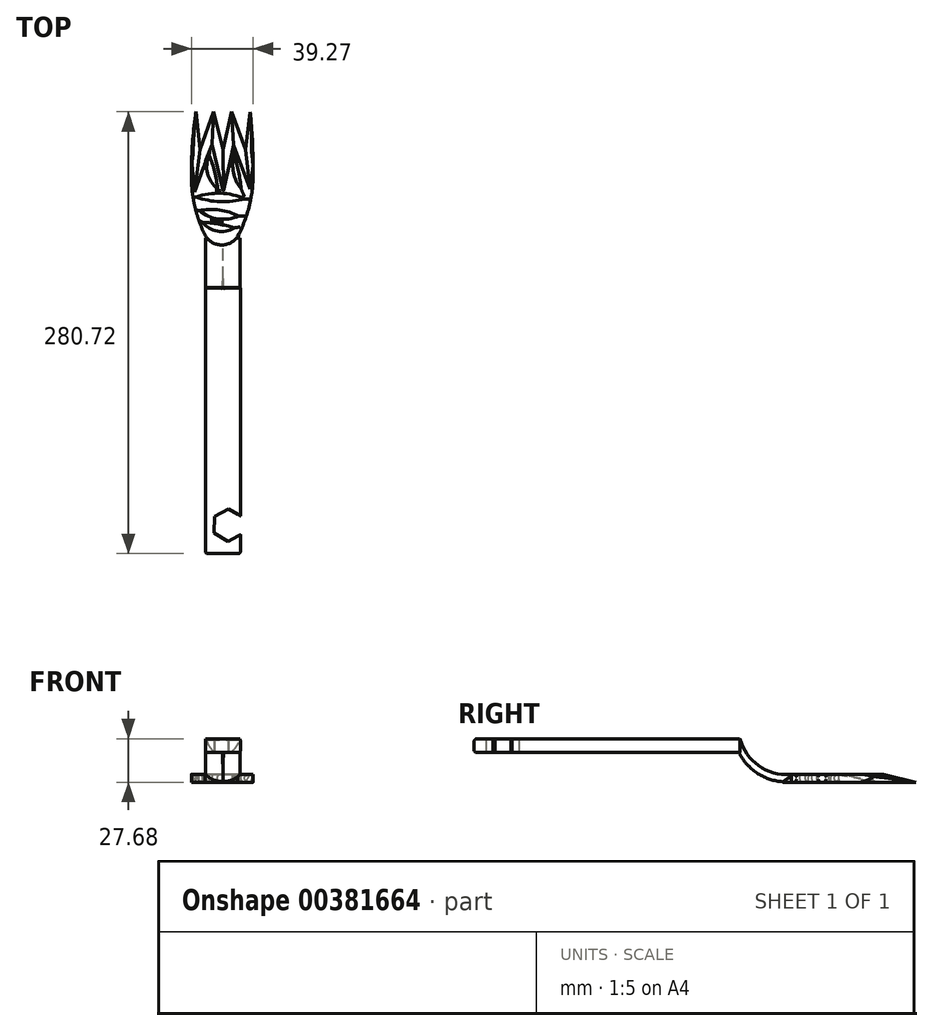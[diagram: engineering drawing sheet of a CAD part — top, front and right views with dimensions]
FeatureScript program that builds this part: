
annotation { "Feature Type Name" : "Feature", "Feature Type Description" : "" }
export const myFeature = defineFeature(function(context is Context, id is Id, definition is map)
    precondition{}
    {
        {
            var Q0;
            Q0=qCreatedBy(makeId("Top.planeOp"),FACE);
            var sketch = newSketch(context, id + "F0", { "sketchPlane" : qUnion([Q0])});
            skArc(sketch, "E0", {"start": v(-17.06, 76.18) * mm, "mid": v(-19.16, 58.5) * mm, "end": v(-19.86, 40.7) * mm});
            skArc(sketch, "E1", {"start": v(19.16, 40.7) * mm, "mid": v(18.71, 58.34) * mm, "end": v(17.35, 75.93) * mm});
            skLineSegment(sketch, "E2", {"start": v(-17.06, 76.18) * mm, "end": v(-14.55, 52.2) * mm});
            skLineSegment(sketch, "E3", {"start": v(14.3, 52.2) * mm, "end": v(17.35, 75.93) * mm});
            skLineSegment(sketch, "E4", {"start": v(-14.55, 52.2) * mm, "end": v(-5.87, 76.18) * mm});
            skLineSegment(sketch, "E5", {"start": v(-5.87, 76.18) * mm, "end": v(0, 52.2) * mm});
            skLineSegment(sketch, "E6", {"start": v(0, 52.2) * mm, "end": v(5.36, 76.18) * mm});
            skLineSegment(sketch, "E7", {"start": v(5.36, 76.18) * mm, "end": v(14.3, 52.2) * mm});
            skPoint(sketch, "E8.startSnap0", {"position": v(-19.86, 40.96) * mm});
            skPoint(sketch, "E9.orphan", {"position": v(19.16, 40.7) * mm});
            skArc(sketch, "E10", {"start": v(9.44, -3.2) * mm, "mid": v(17.18, 18.12) * mm, "end": v(19.16, 40.7) * mm});
            skArc(sketch, "E11", {"start": v(-19.86, 40.7) * mm, "mid": v(-18.37, 18.45) * mm, "end": v(-11.23, -2.68) * mm});
            skArc(sketch, "E12", {"start": v(-11.23, -2.68) * mm, "mid": v(-1.03, -8.6) * mm, "end": v(9.44, -3.2) * mm});
            skSolve(sketch);
        }
        {
            var Q0;
            Q0 = qSketchRegion(id + "F0", true);
            extrude(context, id + "F1", {"entities" : qUnion([Q0]), "endBound" : BoundingType.SYMMETRIC, "depth" : 5.08 * mm});
        }
        {
            var Q0;
            Q0=makeQuery(id+"F1.opExtrude","CAP_EDGE",EDGE,{"disambiguationData":[OSD([sQuery(id+"F0.wireOp",EDGE,"E1")])],"isStart":false});
            var Q1;
            Q1=makeQuery(id+"F1.opExtrude","CAP_EDGE",EDGE,{"disambiguationData":[OSD([sQuery(id+"F0.wireOp",EDGE,"E7")])],"isStart":false});
            var Q2;
            Q2=makeQuery(id+"F1.opExtrude","CAP_EDGE",EDGE,{"disambiguationData":[OSD([sQuery(id+"F0.wireOp",EDGE,"E3")])],"isStart":false});
            var Q3;
            Q3=makeQuery(id+"F1.opExtrude","CAP_EDGE",EDGE,{"disambiguationData":[OSD([sQuery(id+"F0.wireOp",EDGE,"E6")])],"isStart":false});
            var Q4;
            Q4=makeQuery(id+"F1.opExtrude","CAP_EDGE",EDGE,{"disambiguationData":[OSD([sQuery(id+"F0.wireOp",EDGE,"E5")])],"isStart":false});
            var Q5;
            Q5=makeQuery(id+"F1.opExtrude","CAP_EDGE",EDGE,{"disambiguationData":[OSD([sQuery(id+"F0.wireOp",EDGE,"E4")])],"isStart":false});
            var Q6;
            Q6=makeQuery(id+"F1.opExtrude","CAP_EDGE",EDGE,{"disambiguationData":[OSD([sQuery(id+"F0.wireOp",EDGE,"E2")])],"isStart":false});
            var Q7;
            Q7=makeQuery(id+"F1.opExtrude","CAP_EDGE",EDGE,{"disambiguationData":[OSD([sQuery(id+"F0.wireOp",EDGE,"E0")])],"isStart":false});
            chamfer(context, id + "F2", {"entities" : qUnion([Q0, Q1, Q2, Q3, Q4, Q5, Q6, Q7]), "chamferType" : ChamferType.TWO_OFFSETS, "width1" : 5.08 * mm, "oppositeDirection" : true, "width2" : 1.02 * mm, "tangentPropagation" : true});
        }
        {
            var Q0;
            {var subQ0=sQuery(id+"F0.wireOp",EDGE,"E5");Q0=makeQuery(id+"F2.opChamfer","BLEND_EDGE",EDGE,{"blendedFrom":[makeQuery(id+"F1.opExtrude","CAP_EDGE",EDGE,{"disambiguationData":[OSD([subQ0])],"isStart":false}),makeQuery(id+"F1.opExtrude","CAP_FACE",FACE,{"disambiguationData":[OSD([sQuery(id+"F0.wireOp",EDGE,"E0"),sQuery(id+"F0.wireOp",EDGE,"E1"),sQuery(id+"F0.wireOp",EDGE,"E2"),sQuery(id+"F0.wireOp",EDGE,"E3"),sQuery(id+"F0.wireOp",EDGE,"E4"),subQ0,sQuery(id+"F0.wireOp",EDGE,"E6"),sQuery(id+"F0.wireOp",EDGE,"E7"),sQuery(id+"F0.wireOp",EDGE,"E10"),sQuery(id+"F0.wireOp",EDGE,"E11"),sQuery(id+"F0.wireOp",EDGE,"E12")])],"isStart":false})],"blendedInto":[makeQuery(id+"F1.opExtrude","CAP_FACE",FACE,{"disambiguationData":[OSD([sQuery(id+"F0.wireOp",EDGE,"E0"),sQuery(id+"F0.wireOp",EDGE,"E1"),sQuery(id+"F0.wireOp",EDGE,"E2"),sQuery(id+"F0.wireOp",EDGE,"E3"),sQuery(id+"F0.wireOp",EDGE,"E4"),subQ0,sQuery(id+"F0.wireOp",EDGE,"E6"),sQuery(id+"F0.wireOp",EDGE,"E7"),sQuery(id+"F0.wireOp",EDGE,"E10"),sQuery(id+"F0.wireOp",EDGE,"E11"),sQuery(id+"F0.wireOp",EDGE,"E12")])],"isStart":false})]});}
            var Q1;
            {var subQ0=sQuery(id+"F0.wireOp",EDGE,"E4");Q1=makeQuery(id+"F2.opChamfer","BLEND_EDGE",EDGE,{"blendedFrom":[makeQuery(id+"F1.opExtrude","CAP_EDGE",EDGE,{"disambiguationData":[OSD([subQ0])],"isStart":false}),makeQuery(id+"F1.opExtrude","CAP_FACE",FACE,{"disambiguationData":[OSD([sQuery(id+"F0.wireOp",EDGE,"E0"),sQuery(id+"F0.wireOp",EDGE,"E1"),sQuery(id+"F0.wireOp",EDGE,"E2"),sQuery(id+"F0.wireOp",EDGE,"E3"),subQ0,sQuery(id+"F0.wireOp",EDGE,"E5"),sQuery(id+"F0.wireOp",EDGE,"E6"),sQuery(id+"F0.wireOp",EDGE,"E7"),sQuery(id+"F0.wireOp",EDGE,"E10"),sQuery(id+"F0.wireOp",EDGE,"E11"),sQuery(id+"F0.wireOp",EDGE,"E12")])],"isStart":false})],"blendedInto":[makeQuery(id+"F1.opExtrude","CAP_FACE",FACE,{"disambiguationData":[OSD([sQuery(id+"F0.wireOp",EDGE,"E0"),sQuery(id+"F0.wireOp",EDGE,"E1"),sQuery(id+"F0.wireOp",EDGE,"E2"),sQuery(id+"F0.wireOp",EDGE,"E3"),subQ0,sQuery(id+"F0.wireOp",EDGE,"E5"),sQuery(id+"F0.wireOp",EDGE,"E6"),sQuery(id+"F0.wireOp",EDGE,"E7"),sQuery(id+"F0.wireOp",EDGE,"E10"),sQuery(id+"F0.wireOp",EDGE,"E11"),sQuery(id+"F0.wireOp",EDGE,"E12")])],"isStart":false})]});}
            var Q2;
            {var subQ0=sQuery(id+"F0.wireOp",EDGE,"E6");Q2=makeQuery(id+"F2.opChamfer","BLEND_EDGE",EDGE,{"blendedFrom":[makeQuery(id+"F1.opExtrude","CAP_EDGE",EDGE,{"disambiguationData":[OSD([subQ0])],"isStart":false}),makeQuery(id+"F1.opExtrude","CAP_FACE",FACE,{"disambiguationData":[OSD([sQuery(id+"F0.wireOp",EDGE,"E0"),sQuery(id+"F0.wireOp",EDGE,"E1"),sQuery(id+"F0.wireOp",EDGE,"E2"),sQuery(id+"F0.wireOp",EDGE,"E3"),sQuery(id+"F0.wireOp",EDGE,"E4"),sQuery(id+"F0.wireOp",EDGE,"E5"),subQ0,sQuery(id+"F0.wireOp",EDGE,"E7"),sQuery(id+"F0.wireOp",EDGE,"E10"),sQuery(id+"F0.wireOp",EDGE,"E11"),sQuery(id+"F0.wireOp",EDGE,"E12")])],"isStart":false})],"blendedInto":[makeQuery(id+"F1.opExtrude","CAP_FACE",FACE,{"disambiguationData":[OSD([sQuery(id+"F0.wireOp",EDGE,"E0"),sQuery(id+"F0.wireOp",EDGE,"E1"),sQuery(id+"F0.wireOp",EDGE,"E2"),sQuery(id+"F0.wireOp",EDGE,"E3"),sQuery(id+"F0.wireOp",EDGE,"E4"),sQuery(id+"F0.wireOp",EDGE,"E5"),subQ0,sQuery(id+"F0.wireOp",EDGE,"E7"),sQuery(id+"F0.wireOp",EDGE,"E10"),sQuery(id+"F0.wireOp",EDGE,"E11"),sQuery(id+"F0.wireOp",EDGE,"E12")])],"isStart":false})]});}
            var Q3;
            {var subQ0=sQuery(id+"F0.wireOp",EDGE,"E7");Q3=makeQuery(id+"F2.opChamfer","BLEND_EDGE",EDGE,{"blendedFrom":[makeQuery(id+"F1.opExtrude","CAP_EDGE",EDGE,{"disambiguationData":[OSD([subQ0])],"isStart":false}),makeQuery(id+"F1.opExtrude","CAP_FACE",FACE,{"disambiguationData":[OSD([sQuery(id+"F0.wireOp",EDGE,"E0"),sQuery(id+"F0.wireOp",EDGE,"E1"),sQuery(id+"F0.wireOp",EDGE,"E2"),sQuery(id+"F0.wireOp",EDGE,"E3"),sQuery(id+"F0.wireOp",EDGE,"E4"),sQuery(id+"F0.wireOp",EDGE,"E5"),sQuery(id+"F0.wireOp",EDGE,"E6"),subQ0,sQuery(id+"F0.wireOp",EDGE,"E10"),sQuery(id+"F0.wireOp",EDGE,"E11"),sQuery(id+"F0.wireOp",EDGE,"E12")])],"isStart":false})],"blendedInto":[makeQuery(id+"F1.opExtrude","CAP_FACE",FACE,{"disambiguationData":[OSD([sQuery(id+"F0.wireOp",EDGE,"E0"),sQuery(id+"F0.wireOp",EDGE,"E1"),sQuery(id+"F0.wireOp",EDGE,"E2"),sQuery(id+"F0.wireOp",EDGE,"E3"),sQuery(id+"F0.wireOp",EDGE,"E4"),sQuery(id+"F0.wireOp",EDGE,"E5"),sQuery(id+"F0.wireOp",EDGE,"E6"),subQ0,sQuery(id+"F0.wireOp",EDGE,"E10"),sQuery(id+"F0.wireOp",EDGE,"E11"),sQuery(id+"F0.wireOp",EDGE,"E12")])],"isStart":false})]});}
            var Q4;
            {var subQ0=sQuery(id+"F0.wireOp",EDGE,"E3");Q4=makeQuery(id+"F2.opChamfer","BLEND_EDGE",EDGE,{"blendedFrom":[makeQuery(id+"F1.opExtrude","CAP_EDGE",EDGE,{"disambiguationData":[OSD([subQ0])],"isStart":false}),makeQuery(id+"F1.opExtrude","CAP_FACE",FACE,{"disambiguationData":[OSD([sQuery(id+"F0.wireOp",EDGE,"E0"),sQuery(id+"F0.wireOp",EDGE,"E1"),sQuery(id+"F0.wireOp",EDGE,"E2"),subQ0,sQuery(id+"F0.wireOp",EDGE,"E4"),sQuery(id+"F0.wireOp",EDGE,"E5"),sQuery(id+"F0.wireOp",EDGE,"E6"),sQuery(id+"F0.wireOp",EDGE,"E7"),sQuery(id+"F0.wireOp",EDGE,"E10"),sQuery(id+"F0.wireOp",EDGE,"E11"),sQuery(id+"F0.wireOp",EDGE,"E12")])],"isStart":false})],"blendedInto":[makeQuery(id+"F1.opExtrude","CAP_FACE",FACE,{"disambiguationData":[OSD([sQuery(id+"F0.wireOp",EDGE,"E0"),sQuery(id+"F0.wireOp",EDGE,"E1"),sQuery(id+"F0.wireOp",EDGE,"E2"),subQ0,sQuery(id+"F0.wireOp",EDGE,"E4"),sQuery(id+"F0.wireOp",EDGE,"E5"),sQuery(id+"F0.wireOp",EDGE,"E6"),sQuery(id+"F0.wireOp",EDGE,"E7"),sQuery(id+"F0.wireOp",EDGE,"E10"),sQuery(id+"F0.wireOp",EDGE,"E11"),sQuery(id+"F0.wireOp",EDGE,"E12")])],"isStart":false})]});}
            var Q5;
            {var subQ0=sQuery(id+"F0.wireOp",EDGE,"E2");Q5=makeQuery(id+"F2.opChamfer","BLEND_EDGE",EDGE,{"blendedFrom":[makeQuery(id+"F1.opExtrude","CAP_EDGE",EDGE,{"disambiguationData":[OSD([subQ0])],"isStart":false}),makeQuery(id+"F1.opExtrude","CAP_FACE",FACE,{"disambiguationData":[OSD([sQuery(id+"F0.wireOp",EDGE,"E0"),sQuery(id+"F0.wireOp",EDGE,"E1"),subQ0,sQuery(id+"F0.wireOp",EDGE,"E3"),sQuery(id+"F0.wireOp",EDGE,"E4"),sQuery(id+"F0.wireOp",EDGE,"E5"),sQuery(id+"F0.wireOp",EDGE,"E6"),sQuery(id+"F0.wireOp",EDGE,"E7"),sQuery(id+"F0.wireOp",EDGE,"E10"),sQuery(id+"F0.wireOp",EDGE,"E11"),sQuery(id+"F0.wireOp",EDGE,"E12")])],"isStart":false})],"blendedInto":[makeQuery(id+"F1.opExtrude","CAP_FACE",FACE,{"disambiguationData":[OSD([sQuery(id+"F0.wireOp",EDGE,"E0"),sQuery(id+"F0.wireOp",EDGE,"E1"),subQ0,sQuery(id+"F0.wireOp",EDGE,"E3"),sQuery(id+"F0.wireOp",EDGE,"E4"),sQuery(id+"F0.wireOp",EDGE,"E5"),sQuery(id+"F0.wireOp",EDGE,"E6"),sQuery(id+"F0.wireOp",EDGE,"E7"),sQuery(id+"F0.wireOp",EDGE,"E10"),sQuery(id+"F0.wireOp",EDGE,"E11"),sQuery(id+"F0.wireOp",EDGE,"E12")])],"isStart":false})]});}
            chamfer(context, id + "F3", {"entities" : qUnion([Q0, Q1, Q2, Q3, Q4, Q5]), "chamferType" : ChamferType.OFFSET_ANGLE, "width" : 5.08 * mm, "oppositeDirection" : false, "angle" : 40 * degree, "tangentPropagation" : true});
        }
        {
            var Q0;
            Q0=qCreatedBy(makeId("Right.planeOp"),FACE);
            var sketch = newSketch(context, id + "F4", { "sketchPlane" : qUnion([Q0])});
            skArc(sketch, "E13", {"start": v(-36.75, 16.97) * mm, "mid": v(-23.48, 2.4) * mm, "end": v(-4.31, -2.22) * mm});
            skArc(sketch, "E14", {"start": v(-35.73, 25.14) * mm, "mid": v(-24, 8.07) * mm, "end": v(-4.07, 2.39) * mm});
            skLineSegment(sketch, "E15", {"start": v(-35.73, 25.14) * mm, "end": v(-36.75, 16.97) * mm});
            skLineSegment(sketch, "E16", {"start": v(-4.07, 2.39) * mm, "end": v(-4.31, -2.22) * mm});
            skSolve(sketch);
        }
        {
            var Q0;
            Q0 = qSketchRegion(id + "F4", true);
            extrude(context, id + "F5", {"entities" : qUnion([Q0]), "operationType" : NewBodyOperationType.ADD, "endBound" : BoundingType.SYMMETRIC, "depth" : 21.84 * mm});
        }
        {
            var Q0;
            Q0=qCreatedBy(makeId("Right.planeOp"),FACE);
            var sketch = newSketch(context, id + "F6", { "sketchPlane" : qUnion([Q0])});
            skLineSegment(sketch, "E17.bottom", {"start": v(-35.8, 24.94) * mm, "end": v(-204.68, 24.94) * mm});
            skLineSegment(sketch, "E17.top", {"start": v(-35.8, 16.37) * mm, "end": v(-204.68, 16.37) * mm});
            skLineSegment(sketch, "E17.left", {"start": v(-35.8, 24.94) * mm, "end": v(-35.8, 16.37) * mm});
            skLineSegment(sketch, "E17.right", {"start": v(-204.68, 24.94) * mm, "end": v(-204.68, 16.37) * mm});
            skSolve(sketch);
        }
        {
            var Q0;
            Q0 = qSketchRegion(id + "F6", true);
            extrude(context, id + "F7", {"entities" : qUnion([Q0]), "operationType" : NewBodyOperationType.ADD, "endBound" : BoundingType.SYMMETRIC, "depth" : 22.35 * mm});
        }
        {
            var Q0;
            Q0=makeQuery(id+"F5.opExtrude","CAP_EDGE",EDGE,{"disambiguationData":[OSD([sQuery(id+"F4.wireOp",EDGE,"E13")])],"isStart":true});
            var Q1;
            Q1=makeQuery(id+"F5.opExtrude","CAP_EDGE",EDGE,{"disambiguationData":[OSD([sQuery(id+"F4.wireOp",EDGE,"E13")])],"isStart":false});
            fillet(context, id + "F8", {"entities" : qUnion([Q0, Q1]), "radius" : 15.94 * mm, "tangentPropagation" : true, "allowEdgeOverflow" : false});
        }
        {
            var Q0;
            Q0=makeQuery(id+"F7.opExtrude","CAP_EDGE",EDGE,{"disambiguationData":[OSD([sQuery(id+"F6.wireOp",EDGE,"E17.bottom")])],"isStart":false});
            var Q1;
            Q1=makeQuery(id+"F7.opExtrude","CAP_EDGE",EDGE,{"disambiguationData":[OSD([sQuery(id+"F6.wireOp",EDGE,"E17.top")])],"isStart":false});
            var Q2;
            Q2=makeQuery(id+"F7.opExtrude","CAP_EDGE",EDGE,{"disambiguationData":[OSD([sQuery(id+"F6.wireOp",EDGE,"E17.bottom")])],"isStart":true});
            var Q3;
            Q3=makeQuery(id+"F7.opExtrude","CAP_EDGE",EDGE,{"disambiguationData":[OSD([sQuery(id+"F6.wireOp",EDGE,"E17.top")])],"isStart":true});
            var Q4;
            Q4=makeQuery(id+"F7.opExtrude","SWEPT_FACE",FACE,{"disambiguationData":[OSD([sQuery(id+"F6.wireOp",EDGE,"E17.right")])]});
            fillet(context, id + "F9", {"entities" : qUnion([Q0, Q1, Q2, Q3, Q4]), "radius" : 1.55 * mm, "tangentPropagation" : true, "allowEdgeOverflow" : false});
        }
        {
            var Q0;
            Q0=makeQuery(id+"F9.opFillet","BLEND_EDGE",EDGE,{"blendedFrom":[makeQuery(id+"F7.opExtrude","CAP_EDGE",EDGE,{"disambiguationData":[OSD([sQuery(id+"F6.wireOp",EDGE,"E17.top")])],"isStart":false}),makeQuery(id+"F7.opExtrude","SWEPT_FACE",FACE,{"disambiguationData":[OSD([sQuery(id+"F6.wireOp",EDGE,"E17.left")])]})],"blendedInto":[makeQuery(id+"F7.opExtrude","SWEPT_FACE",FACE,{"disambiguationData":[OSD([sQuery(id+"F6.wireOp",EDGE,"E17.left")])]})]});
            var Q1;
            Q1=makeQuery(id+"F9.opFillet","BLEND_EDGE",EDGE,{"blendedFrom":[makeQuery(id+"F7.opExtrude","CAP_EDGE",EDGE,{"disambiguationData":[OSD([sQuery(id+"F6.wireOp",EDGE,"E17.top")])],"isStart":true}),makeQuery(id+"F7.opExtrude","SWEPT_FACE",FACE,{"disambiguationData":[OSD([sQuery(id+"F6.wireOp",EDGE,"E17.left")])]})],"blendedInto":[makeQuery(id+"F7.opExtrude","SWEPT_FACE",FACE,{"disambiguationData":[OSD([sQuery(id+"F6.wireOp",EDGE,"E17.left")])]})]});
            fillet(context, id + "F10", {"entities" : qUnion([Q0, Q1]), "radius" : 0.5 * mm, "tangentPropagation" : true, "allowEdgeOverflow" : false});
        }
        {
            var Q0;
            Q0=qCreatedBy(makeId("Top.planeOp"),FACE);
            var sketch = newSketch(context, id + "F11", { "sketchPlane" : qUnion([Q0])});
            skArc(sketch, "E18", {"start": v(13.88, 20.7) * mm, "mid": v(-1.4, 24.24) * mm, "end": v(-16.91, 21.85) * mm});
            skArc(sketch, "E19", {"start": v(-16.91, 21.85) * mm, "mid": v(-1.6, 18.87) * mm, "end": v(13.88, 20.7) * mm});
            skArc(sketch, "E20", {"start": v(-8.66, 48.42) * mm, "mid": v(-9.75, 36.88) * mm, "end": v(-3.36, 27.2) * mm});
            skArc(sketch, "E21", {"start": v(-3.36, 27.2) * mm, "mid": v(-5.31, 37.99) * mm, "end": v(-8.66, 48.42) * mm});
            skArc(sketch, "E22", {"start": v(11.5, 27.2) * mm, "mid": v(9.97, 37.95) * mm, "end": v(7.14, 48.42) * mm});
            skArc(sketch, "E23", {"start": v(7.14, 48.42) * mm, "mid": v(6.72, 37.28) * mm, "end": v(11.5, 27.2) * mm});
            skArc(sketch, "E24", {"start": v(-15.07, 13.17) * mm, "mid": v(-2.94, 7.96) * mm, "end": v(10.12, 9.84) * mm});
            skArc(sketch, "E25", {"start": v(10.12, 9.84) * mm, "mid": v(-2.2, 13.6) * mm, "end": v(-15.07, 13.17) * mm});
            skArc(sketch, "E26", {"start": v(-12.9, 5.76) * mm, "mid": v(-3.55, 0.2) * mm, "end": v(7.14, 2.27) * mm});
            skArc(sketch, "E27", {"start": v(7.14, 2.27) * mm, "mid": v(-2.77, 4.68) * mm, "end": v(-12.9, 5.76) * mm});
            skSolve(sketch);
        }
        {
            var Q0;
            Q0 = qSketchRegion(id + "F11", true);
            extrude(context, id + "F12", {"entities" : qUnion([Q0]), "operationType" : NewBodyOperationType.REMOVE, "endBound" : BoundingType.SYMMETRIC, "oppositeDirection" : true, "depth" : 25.4 * mm});
        }
        {
            var Q0;
            Q0=makeQuery(id+"F12.boolean.opBoolean","INTERSECT",EDGE,{"derivedFrom":[makeQuery(id+"F1.opExtrude","CAP_FACE",FACE,{"disambiguationData":[OSD([sQuery(id+"F0.wireOp",EDGE,"E0"),sQuery(id+"F0.wireOp",EDGE,"E1"),sQuery(id+"F0.wireOp",EDGE,"E2"),sQuery(id+"F0.wireOp",EDGE,"E3"),sQuery(id+"F0.wireOp",EDGE,"E4"),sQuery(id+"F0.wireOp",EDGE,"E5"),sQuery(id+"F0.wireOp",EDGE,"E6"),sQuery(id+"F0.wireOp",EDGE,"E7"),sQuery(id+"F0.wireOp",EDGE,"E10"),sQuery(id+"F0.wireOp",EDGE,"E11"),sQuery(id+"F0.wireOp",EDGE,"E12")])],"isStart":false}),makeQuery(id+"F12.opExtrude","SWEPT_FACE",FACE,{"disambiguationData":[OSD([sQuery(id+"F11.wireOp",EDGE,"E20")])]})]});
            var Q1;
            Q1=makeQuery(id+"F12.boolean.opBoolean","INTERSECT",EDGE,{"derivedFrom":[makeQuery(id+"F1.opExtrude","CAP_FACE",FACE,{"disambiguationData":[OSD([sQuery(id+"F0.wireOp",EDGE,"E0"),sQuery(id+"F0.wireOp",EDGE,"E1"),sQuery(id+"F0.wireOp",EDGE,"E2"),sQuery(id+"F0.wireOp",EDGE,"E3"),sQuery(id+"F0.wireOp",EDGE,"E4"),sQuery(id+"F0.wireOp",EDGE,"E5"),sQuery(id+"F0.wireOp",EDGE,"E6"),sQuery(id+"F0.wireOp",EDGE,"E7"),sQuery(id+"F0.wireOp",EDGE,"E10"),sQuery(id+"F0.wireOp",EDGE,"E11"),sQuery(id+"F0.wireOp",EDGE,"E12")])],"isStart":false}),makeQuery(id+"F12.opExtrude","SWEPT_FACE",FACE,{"disambiguationData":[OSD([sQuery(id+"F11.wireOp",EDGE,"E21")])]})]});
            var Q2;
            Q2=makeQuery(id+"F12.boolean.opBoolean","INTERSECT",EDGE,{"derivedFrom":[makeQuery(id+"F1.opExtrude","CAP_FACE",FACE,{"disambiguationData":[OSD([sQuery(id+"F0.wireOp",EDGE,"E0"),sQuery(id+"F0.wireOp",EDGE,"E1"),sQuery(id+"F0.wireOp",EDGE,"E2"),sQuery(id+"F0.wireOp",EDGE,"E3"),sQuery(id+"F0.wireOp",EDGE,"E4"),sQuery(id+"F0.wireOp",EDGE,"E5"),sQuery(id+"F0.wireOp",EDGE,"E6"),sQuery(id+"F0.wireOp",EDGE,"E7"),sQuery(id+"F0.wireOp",EDGE,"E10"),sQuery(id+"F0.wireOp",EDGE,"E11"),sQuery(id+"F0.wireOp",EDGE,"E12")])],"isStart":false}),makeQuery(id+"F12.opExtrude","SWEPT_FACE",FACE,{"disambiguationData":[OSD([sQuery(id+"F11.wireOp",EDGE,"E22")])]})]});
            var Q3;
            Q3=makeQuery(id+"F12.boolean.opBoolean","INTERSECT",EDGE,{"derivedFrom":[makeQuery(id+"F1.opExtrude","CAP_FACE",FACE,{"disambiguationData":[OSD([sQuery(id+"F0.wireOp",EDGE,"E0"),sQuery(id+"F0.wireOp",EDGE,"E1"),sQuery(id+"F0.wireOp",EDGE,"E2"),sQuery(id+"F0.wireOp",EDGE,"E3"),sQuery(id+"F0.wireOp",EDGE,"E4"),sQuery(id+"F0.wireOp",EDGE,"E5"),sQuery(id+"F0.wireOp",EDGE,"E6"),sQuery(id+"F0.wireOp",EDGE,"E7"),sQuery(id+"F0.wireOp",EDGE,"E10"),sQuery(id+"F0.wireOp",EDGE,"E11"),sQuery(id+"F0.wireOp",EDGE,"E12")])],"isStart":false}),makeQuery(id+"F12.opExtrude","SWEPT_FACE",FACE,{"disambiguationData":[OSD([sQuery(id+"F11.wireOp",EDGE,"E23")])]})]});
            var Q4;
            Q4=makeQuery(id+"F12.boolean.opBoolean","INTERSECT",EDGE,{"derivedFrom":[makeQuery(id+"F1.opExtrude","CAP_FACE",FACE,{"disambiguationData":[OSD([sQuery(id+"F0.wireOp",EDGE,"E0"),sQuery(id+"F0.wireOp",EDGE,"E1"),sQuery(id+"F0.wireOp",EDGE,"E2"),sQuery(id+"F0.wireOp",EDGE,"E3"),sQuery(id+"F0.wireOp",EDGE,"E4"),sQuery(id+"F0.wireOp",EDGE,"E5"),sQuery(id+"F0.wireOp",EDGE,"E6"),sQuery(id+"F0.wireOp",EDGE,"E7"),sQuery(id+"F0.wireOp",EDGE,"E10"),sQuery(id+"F0.wireOp",EDGE,"E11"),sQuery(id+"F0.wireOp",EDGE,"E12")])],"isStart":false}),makeQuery(id+"F12.opExtrude","SWEPT_FACE",FACE,{"disambiguationData":[OSD([sQuery(id+"F11.wireOp",EDGE,"E19")])]})]});
            var Q5;
            Q5=makeQuery(id+"F12.boolean.opBoolean","INTERSECT",EDGE,{"derivedFrom":[makeQuery(id+"F1.opExtrude","CAP_FACE",FACE,{"disambiguationData":[OSD([sQuery(id+"F0.wireOp",EDGE,"E0"),sQuery(id+"F0.wireOp",EDGE,"E1"),sQuery(id+"F0.wireOp",EDGE,"E2"),sQuery(id+"F0.wireOp",EDGE,"E3"),sQuery(id+"F0.wireOp",EDGE,"E4"),sQuery(id+"F0.wireOp",EDGE,"E5"),sQuery(id+"F0.wireOp",EDGE,"E6"),sQuery(id+"F0.wireOp",EDGE,"E7"),sQuery(id+"F0.wireOp",EDGE,"E10"),sQuery(id+"F0.wireOp",EDGE,"E11"),sQuery(id+"F0.wireOp",EDGE,"E12")])],"isStart":false}),makeQuery(id+"F12.opExtrude","SWEPT_FACE",FACE,{"disambiguationData":[OSD([sQuery(id+"F11.wireOp",EDGE,"E18")])]})]});
            var Q6;
            Q6=makeQuery(id+"F12.boolean.opBoolean","INTERSECT",EDGE,{"derivedFrom":[makeQuery(id+"F1.opExtrude","CAP_FACE",FACE,{"disambiguationData":[OSD([sQuery(id+"F0.wireOp",EDGE,"E0"),sQuery(id+"F0.wireOp",EDGE,"E1"),sQuery(id+"F0.wireOp",EDGE,"E2"),sQuery(id+"F0.wireOp",EDGE,"E3"),sQuery(id+"F0.wireOp",EDGE,"E4"),sQuery(id+"F0.wireOp",EDGE,"E5"),sQuery(id+"F0.wireOp",EDGE,"E6"),sQuery(id+"F0.wireOp",EDGE,"E7"),sQuery(id+"F0.wireOp",EDGE,"E10"),sQuery(id+"F0.wireOp",EDGE,"E11"),sQuery(id+"F0.wireOp",EDGE,"E12")])],"isStart":false}),makeQuery(id+"F12.opExtrude","SWEPT_FACE",FACE,{"disambiguationData":[OSD([sQuery(id+"F11.wireOp",EDGE,"E25")])]})]});
            var Q7;
            Q7=makeQuery(id+"F12.boolean.opBoolean","INTERSECT",EDGE,{"derivedFrom":[makeQuery(id+"F1.opExtrude","CAP_FACE",FACE,{"disambiguationData":[OSD([sQuery(id+"F0.wireOp",EDGE,"E0"),sQuery(id+"F0.wireOp",EDGE,"E1"),sQuery(id+"F0.wireOp",EDGE,"E2"),sQuery(id+"F0.wireOp",EDGE,"E3"),sQuery(id+"F0.wireOp",EDGE,"E4"),sQuery(id+"F0.wireOp",EDGE,"E5"),sQuery(id+"F0.wireOp",EDGE,"E6"),sQuery(id+"F0.wireOp",EDGE,"E7"),sQuery(id+"F0.wireOp",EDGE,"E10"),sQuery(id+"F0.wireOp",EDGE,"E11"),sQuery(id+"F0.wireOp",EDGE,"E12")])],"isStart":false}),makeQuery(id+"F12.opExtrude","SWEPT_FACE",FACE,{"disambiguationData":[OSD([sQuery(id+"F11.wireOp",EDGE,"E24")])]})]});
            var Q8;
            Q8=makeQuery(id+"F12.boolean.opBoolean","INTERSECT",EDGE,{"derivedFrom":[makeQuery(id+"F1.opExtrude","CAP_FACE",FACE,{"disambiguationData":[OSD([sQuery(id+"F0.wireOp",EDGE,"E0"),sQuery(id+"F0.wireOp",EDGE,"E1"),sQuery(id+"F0.wireOp",EDGE,"E2"),sQuery(id+"F0.wireOp",EDGE,"E3"),sQuery(id+"F0.wireOp",EDGE,"E4"),sQuery(id+"F0.wireOp",EDGE,"E5"),sQuery(id+"F0.wireOp",EDGE,"E6"),sQuery(id+"F0.wireOp",EDGE,"E7"),sQuery(id+"F0.wireOp",EDGE,"E10"),sQuery(id+"F0.wireOp",EDGE,"E11"),sQuery(id+"F0.wireOp",EDGE,"E12")])],"isStart":false}),makeQuery(id+"F12.opExtrude","SWEPT_FACE",FACE,{"disambiguationData":[OSD([sQuery(id+"F11.wireOp",EDGE,"E27")])]})]});
            var Q9;
            Q9=makeQuery(id+"F12.boolean.opBoolean","INTERSECT",EDGE,{"derivedFrom":[makeQuery(id+"F1.opExtrude","CAP_FACE",FACE,{"disambiguationData":[OSD([sQuery(id+"F0.wireOp",EDGE,"E0"),sQuery(id+"F0.wireOp",EDGE,"E1"),sQuery(id+"F0.wireOp",EDGE,"E2"),sQuery(id+"F0.wireOp",EDGE,"E3"),sQuery(id+"F0.wireOp",EDGE,"E4"),sQuery(id+"F0.wireOp",EDGE,"E5"),sQuery(id+"F0.wireOp",EDGE,"E6"),sQuery(id+"F0.wireOp",EDGE,"E7"),sQuery(id+"F0.wireOp",EDGE,"E10"),sQuery(id+"F0.wireOp",EDGE,"E11"),sQuery(id+"F0.wireOp",EDGE,"E12")])],"isStart":false}),makeQuery(id+"F12.opExtrude","SWEPT_FACE",FACE,{"disambiguationData":[OSD([sQuery(id+"F11.wireOp",EDGE,"E26")])]})]});
            var Q10;
            Q10=makeQuery(id+"F12.boolean.opBoolean","INTERSECT",EDGE,{"derivedFrom":[makeQuery(id+"F1.opExtrude","CAP_FACE",FACE,{"disambiguationData":[OSD([sQuery(id+"F0.wireOp",EDGE,"E0"),sQuery(id+"F0.wireOp",EDGE,"E1"),sQuery(id+"F0.wireOp",EDGE,"E2"),sQuery(id+"F0.wireOp",EDGE,"E3"),sQuery(id+"F0.wireOp",EDGE,"E4"),sQuery(id+"F0.wireOp",EDGE,"E5"),sQuery(id+"F0.wireOp",EDGE,"E6"),sQuery(id+"F0.wireOp",EDGE,"E7"),sQuery(id+"F0.wireOp",EDGE,"E10"),sQuery(id+"F0.wireOp",EDGE,"E11"),sQuery(id+"F0.wireOp",EDGE,"E12")])],"isStart":true}),makeQuery(id+"F12.opExtrude","SWEPT_FACE",FACE,{"disambiguationData":[OSD([sQuery(id+"F11.wireOp",EDGE,"E23")])]})]});
            var Q11;
            Q11=makeQuery(id+"F12.boolean.opBoolean","INTERSECT",EDGE,{"derivedFrom":[makeQuery(id+"F1.opExtrude","CAP_FACE",FACE,{"disambiguationData":[OSD([sQuery(id+"F0.wireOp",EDGE,"E0"),sQuery(id+"F0.wireOp",EDGE,"E1"),sQuery(id+"F0.wireOp",EDGE,"E2"),sQuery(id+"F0.wireOp",EDGE,"E3"),sQuery(id+"F0.wireOp",EDGE,"E4"),sQuery(id+"F0.wireOp",EDGE,"E5"),sQuery(id+"F0.wireOp",EDGE,"E6"),sQuery(id+"F0.wireOp",EDGE,"E7"),sQuery(id+"F0.wireOp",EDGE,"E10"),sQuery(id+"F0.wireOp",EDGE,"E11"),sQuery(id+"F0.wireOp",EDGE,"E12")])],"isStart":true}),makeQuery(id+"F12.opExtrude","SWEPT_FACE",FACE,{"disambiguationData":[OSD([sQuery(id+"F11.wireOp",EDGE,"E22")])]})]});
            var Q12;
            Q12=makeQuery(id+"F12.boolean.opBoolean","INTERSECT",EDGE,{"derivedFrom":[makeQuery(id+"F1.opExtrude","CAP_FACE",FACE,{"disambiguationData":[OSD([sQuery(id+"F0.wireOp",EDGE,"E0"),sQuery(id+"F0.wireOp",EDGE,"E1"),sQuery(id+"F0.wireOp",EDGE,"E2"),sQuery(id+"F0.wireOp",EDGE,"E3"),sQuery(id+"F0.wireOp",EDGE,"E4"),sQuery(id+"F0.wireOp",EDGE,"E5"),sQuery(id+"F0.wireOp",EDGE,"E6"),sQuery(id+"F0.wireOp",EDGE,"E7"),sQuery(id+"F0.wireOp",EDGE,"E10"),sQuery(id+"F0.wireOp",EDGE,"E11"),sQuery(id+"F0.wireOp",EDGE,"E12")])],"isStart":true}),makeQuery(id+"F12.opExtrude","SWEPT_FACE",FACE,{"disambiguationData":[OSD([sQuery(id+"F11.wireOp",EDGE,"E21")])]})]});
            var Q13;
            Q13=makeQuery(id+"F12.boolean.opBoolean","INTERSECT",EDGE,{"derivedFrom":[makeQuery(id+"F1.opExtrude","CAP_FACE",FACE,{"disambiguationData":[OSD([sQuery(id+"F0.wireOp",EDGE,"E0"),sQuery(id+"F0.wireOp",EDGE,"E1"),sQuery(id+"F0.wireOp",EDGE,"E2"),sQuery(id+"F0.wireOp",EDGE,"E3"),sQuery(id+"F0.wireOp",EDGE,"E4"),sQuery(id+"F0.wireOp",EDGE,"E5"),sQuery(id+"F0.wireOp",EDGE,"E6"),sQuery(id+"F0.wireOp",EDGE,"E7"),sQuery(id+"F0.wireOp",EDGE,"E10"),sQuery(id+"F0.wireOp",EDGE,"E11"),sQuery(id+"F0.wireOp",EDGE,"E12")])],"isStart":true}),makeQuery(id+"F12.opExtrude","SWEPT_FACE",FACE,{"disambiguationData":[OSD([sQuery(id+"F11.wireOp",EDGE,"E20")])]})]});
            var Q14;
            Q14=makeQuery(id+"F12.boolean.opBoolean","INTERSECT",EDGE,{"derivedFrom":[makeQuery(id+"F1.opExtrude","CAP_FACE",FACE,{"disambiguationData":[OSD([sQuery(id+"F0.wireOp",EDGE,"E0"),sQuery(id+"F0.wireOp",EDGE,"E1"),sQuery(id+"F0.wireOp",EDGE,"E2"),sQuery(id+"F0.wireOp",EDGE,"E3"),sQuery(id+"F0.wireOp",EDGE,"E4"),sQuery(id+"F0.wireOp",EDGE,"E5"),sQuery(id+"F0.wireOp",EDGE,"E6"),sQuery(id+"F0.wireOp",EDGE,"E7"),sQuery(id+"F0.wireOp",EDGE,"E10"),sQuery(id+"F0.wireOp",EDGE,"E11"),sQuery(id+"F0.wireOp",EDGE,"E12")])],"isStart":true}),makeQuery(id+"F12.opExtrude","SWEPT_FACE",FACE,{"disambiguationData":[OSD([sQuery(id+"F11.wireOp",EDGE,"E18")])]})]});
            var Q15;
            Q15=makeQuery(id+"F12.boolean.opBoolean","INTERSECT",EDGE,{"derivedFrom":[makeQuery(id+"F1.opExtrude","CAP_FACE",FACE,{"disambiguationData":[OSD([sQuery(id+"F0.wireOp",EDGE,"E0"),sQuery(id+"F0.wireOp",EDGE,"E1"),sQuery(id+"F0.wireOp",EDGE,"E2"),sQuery(id+"F0.wireOp",EDGE,"E3"),sQuery(id+"F0.wireOp",EDGE,"E4"),sQuery(id+"F0.wireOp",EDGE,"E5"),sQuery(id+"F0.wireOp",EDGE,"E6"),sQuery(id+"F0.wireOp",EDGE,"E7"),sQuery(id+"F0.wireOp",EDGE,"E10"),sQuery(id+"F0.wireOp",EDGE,"E11"),sQuery(id+"F0.wireOp",EDGE,"E12")])],"isStart":true}),makeQuery(id+"F12.opExtrude","SWEPT_FACE",FACE,{"disambiguationData":[OSD([sQuery(id+"F11.wireOp",EDGE,"E19")])]})]});
            var Q16;
            Q16=makeQuery(id+"F12.boolean.opBoolean","INTERSECT",EDGE,{"derivedFrom":[makeQuery(id+"F1.opExtrude","CAP_FACE",FACE,{"disambiguationData":[OSD([sQuery(id+"F0.wireOp",EDGE,"E0"),sQuery(id+"F0.wireOp",EDGE,"E1"),sQuery(id+"F0.wireOp",EDGE,"E2"),sQuery(id+"F0.wireOp",EDGE,"E3"),sQuery(id+"F0.wireOp",EDGE,"E4"),sQuery(id+"F0.wireOp",EDGE,"E5"),sQuery(id+"F0.wireOp",EDGE,"E6"),sQuery(id+"F0.wireOp",EDGE,"E7"),sQuery(id+"F0.wireOp",EDGE,"E10"),sQuery(id+"F0.wireOp",EDGE,"E11"),sQuery(id+"F0.wireOp",EDGE,"E12")])],"isStart":true}),makeQuery(id+"F12.opExtrude","SWEPT_FACE",FACE,{"disambiguationData":[OSD([sQuery(id+"F11.wireOp",EDGE,"E25")])]})]});
            var Q17;
            Q17=makeQuery(id+"F12.boolean.opBoolean","INTERSECT",EDGE,{"derivedFrom":[makeQuery(id+"F1.opExtrude","CAP_FACE",FACE,{"disambiguationData":[OSD([sQuery(id+"F0.wireOp",EDGE,"E0"),sQuery(id+"F0.wireOp",EDGE,"E1"),sQuery(id+"F0.wireOp",EDGE,"E2"),sQuery(id+"F0.wireOp",EDGE,"E3"),sQuery(id+"F0.wireOp",EDGE,"E4"),sQuery(id+"F0.wireOp",EDGE,"E5"),sQuery(id+"F0.wireOp",EDGE,"E6"),sQuery(id+"F0.wireOp",EDGE,"E7"),sQuery(id+"F0.wireOp",EDGE,"E10"),sQuery(id+"F0.wireOp",EDGE,"E11"),sQuery(id+"F0.wireOp",EDGE,"E12")])],"isStart":true}),makeQuery(id+"F12.opExtrude","SWEPT_FACE",FACE,{"disambiguationData":[OSD([sQuery(id+"F11.wireOp",EDGE,"E24")])]})]});
            var Q18;
            Q18=makeQuery(id+"F12.boolean.opBoolean","INTERSECT",EDGE,{"derivedFrom":[makeQuery(id+"F1.opExtrude","CAP_FACE",FACE,{"disambiguationData":[OSD([sQuery(id+"F0.wireOp",EDGE,"E0"),sQuery(id+"F0.wireOp",EDGE,"E1"),sQuery(id+"F0.wireOp",EDGE,"E2"),sQuery(id+"F0.wireOp",EDGE,"E3"),sQuery(id+"F0.wireOp",EDGE,"E4"),sQuery(id+"F0.wireOp",EDGE,"E5"),sQuery(id+"F0.wireOp",EDGE,"E6"),sQuery(id+"F0.wireOp",EDGE,"E7"),sQuery(id+"F0.wireOp",EDGE,"E10"),sQuery(id+"F0.wireOp",EDGE,"E11"),sQuery(id+"F0.wireOp",EDGE,"E12")])],"isStart":true}),makeQuery(id+"F12.opExtrude","SWEPT_FACE",FACE,{"disambiguationData":[OSD([sQuery(id+"F11.wireOp",EDGE,"E26")])]})]});
            var Q19;
            Q19=makeQuery(id+"F12.boolean.opBoolean","INTERSECT",EDGE,{"derivedFrom":[makeQuery(id+"F1.opExtrude","CAP_FACE",FACE,{"disambiguationData":[OSD([sQuery(id+"F0.wireOp",EDGE,"E0"),sQuery(id+"F0.wireOp",EDGE,"E1"),sQuery(id+"F0.wireOp",EDGE,"E2"),sQuery(id+"F0.wireOp",EDGE,"E3"),sQuery(id+"F0.wireOp",EDGE,"E4"),sQuery(id+"F0.wireOp",EDGE,"E5"),sQuery(id+"F0.wireOp",EDGE,"E6"),sQuery(id+"F0.wireOp",EDGE,"E7"),sQuery(id+"F0.wireOp",EDGE,"E10"),sQuery(id+"F0.wireOp",EDGE,"E11"),sQuery(id+"F0.wireOp",EDGE,"E12")])],"isStart":true}),makeQuery(id+"F12.opExtrude","SWEPT_FACE",FACE,{"disambiguationData":[OSD([sQuery(id+"F11.wireOp",EDGE,"E27")])]})]});
            fillet(context, id + "F13", {"entities" : qUnion([Q0, Q1, Q2, Q3, Q4, Q5, Q6, Q7, Q8, Q9, Q10, Q11, Q12, Q13, Q14, Q15, Q16, Q17, Q18, Q19]), "radius" : 1.84 * mm, "tangentPropagation" : true, "allowEdgeOverflow" : false});
        }
        {
            var Q0;
            Q0=qCreatedBy(makeId("Top.planeOp"),FACE);
            var sketch = newSketch(context, id + "F14", { "sketchPlane" : qUnion([Q0])});
            skCircle(sketch, "E28.cCircle", {"center": v(3.45, -186.56) * mm, "radius": 9.03 * mm, "construction": true});
            skLineSegment(sketch, "E28.0", {"start": v(3.2, -196.98) * mm, "end": v(-5.7, -191.55) * mm});
            skLineSegment(sketch, "E28.1", {"start": v(-5.7, -191.55) * mm, "end": v(-5.45, -181.13) * mm});
            skLineSegment(sketch, "E28.2", {"start": v(-5.45, -181.13) * mm, "end": v(3.7, -176.14) * mm});
            skLineSegment(sketch, "E28.3", {"start": v(3.7, -176.14) * mm, "end": v(12.6, -181.57) * mm});
            skLineSegment(sketch, "E28.4", {"start": v(12.6, -181.57) * mm, "end": v(12.34, -192) * mm});
            skLineSegment(sketch, "E28.5", {"start": v(12.34, -192) * mm, "end": v(3.2, -196.98) * mm});
            skPoint(sketch, "E28.0.midPoint", {"position": v(-1.26, -194.26) * mm});
            skSolve(sketch);
        }
        {
            var Q0;
            Q0 = qSketchRegion(id + "F14", true);
            extrude(context, id + "F15", {"entities" : qUnion([Q0]), "operationType" : NewBodyOperationType.REMOVE, "depth" : 25.4 * mm});
        }
    });
